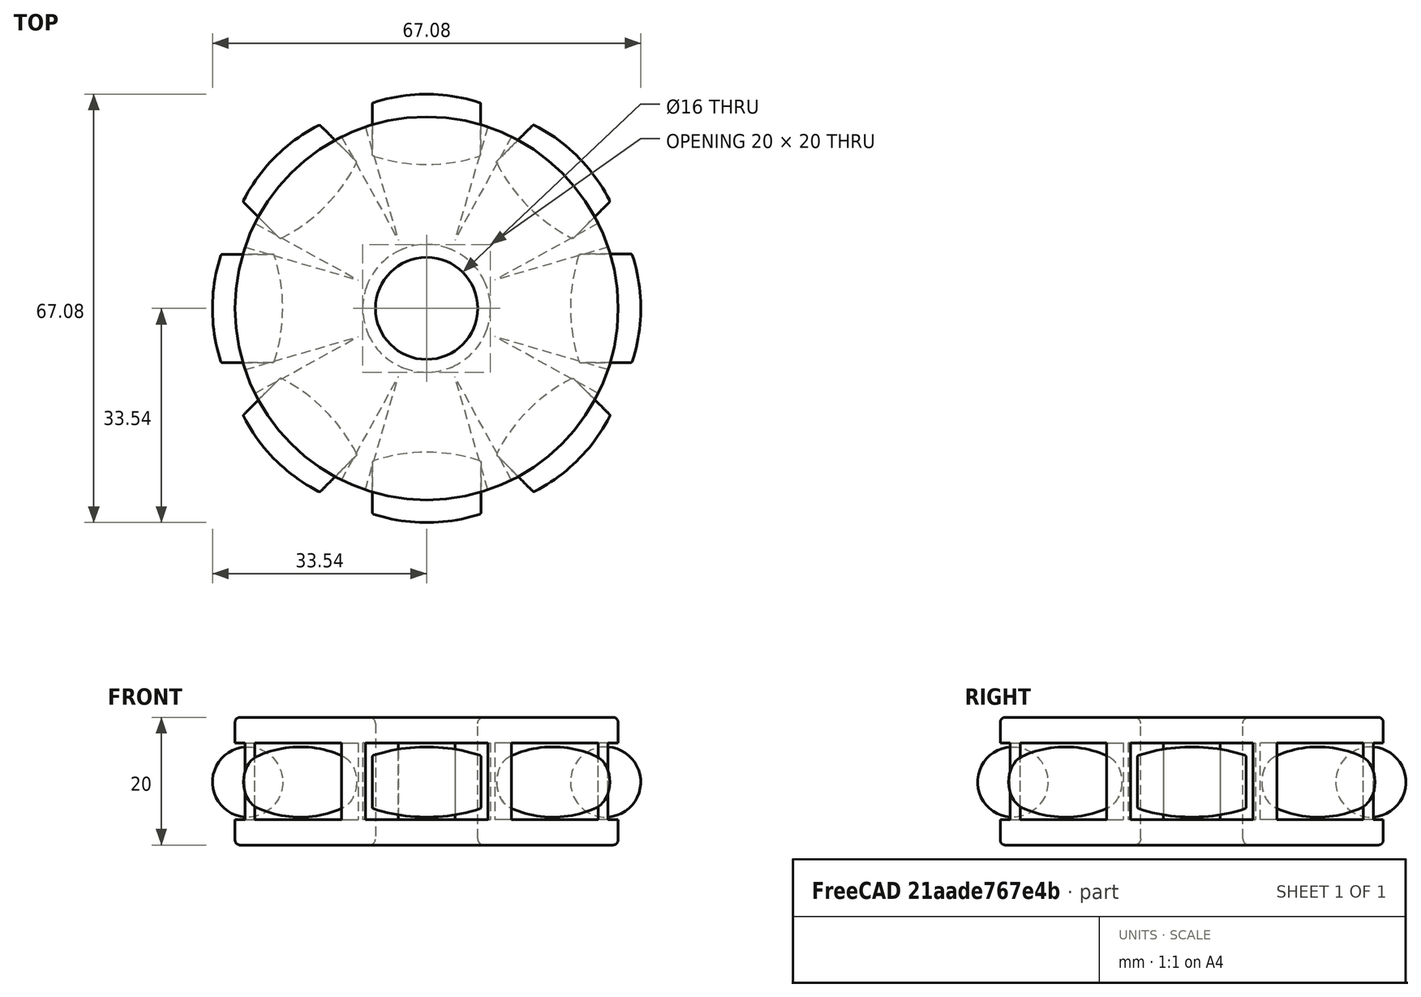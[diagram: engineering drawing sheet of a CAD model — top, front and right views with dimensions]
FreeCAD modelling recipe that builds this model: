
FCSTD DOCUMENT  (FreeCAD 1.0R39319 (Git))
Label: Roda-Omni60_1
License: All rights reserved
LicenseURL: http://en.wikipedia.org/wiki/All_rights_reserved
objects: Part::FeaturePython×3
note: 3 computed .brp shape members not serialized (recipe doc carries the construction recipe); baked Part::Feature solids carry a one-line shape summary decoded from their .brp

FEATURE [Part::FeaturePython] b_Roda_Omnixx_001_  label="Roda-Omnixx_001"  # a2plus imported part (geometry in sourceFile) (typed FeaturePython)
  Placement = pos=(0,0,0) rot=(0.57735,-0.57735,-0.57735;4.18879rad)
  a2p_Version = 0.4.68
  fixedPosition = true
  objectType = a2pPart
  sourceFile = ./Omni-Center.FCStd
  subassemblyImport = false
  timeLastImport = 1.76417e+09
  updateColors = true
FEATURE [Part::FeaturePython] b_Omni_Ball_001_  label="Omni-Ball_001"  # a2plus imported part (geometry in sourceFile) (typed FeaturePython)
  Placement = pos=(28.0377,0.0137478,-0.131092) rot=(0,0.707107,0.707107;3.14159rad)
  a2p_Version = V0.1
  fixedPosition = false
  objectType = a2pPart
  sourceFile = .\Omni-Ball.FCStd
  subassemblyImport = false
  timeLastImport = 1.5747e+09
  updateColors = true
FEATURE [Part::FeaturePython] Array  # Draft array (typed FeaturePython)
  Angle = 360
  ArrayType = 1
  Axis = (0,0,1)
  Base = -> b_Omni_Ball_001_
  Center = (0,0,0)
  Count = 8
  Fuse = false
  IntervalAxis = (0,0,0)
  IntervalX = (1,0,0)
  IntervalY = (0,1,0)
  IntervalZ = (0,0,1)
  NumberPolar = 8
  NumberX = 2
  NumberY = 2
  NumberZ = 1
